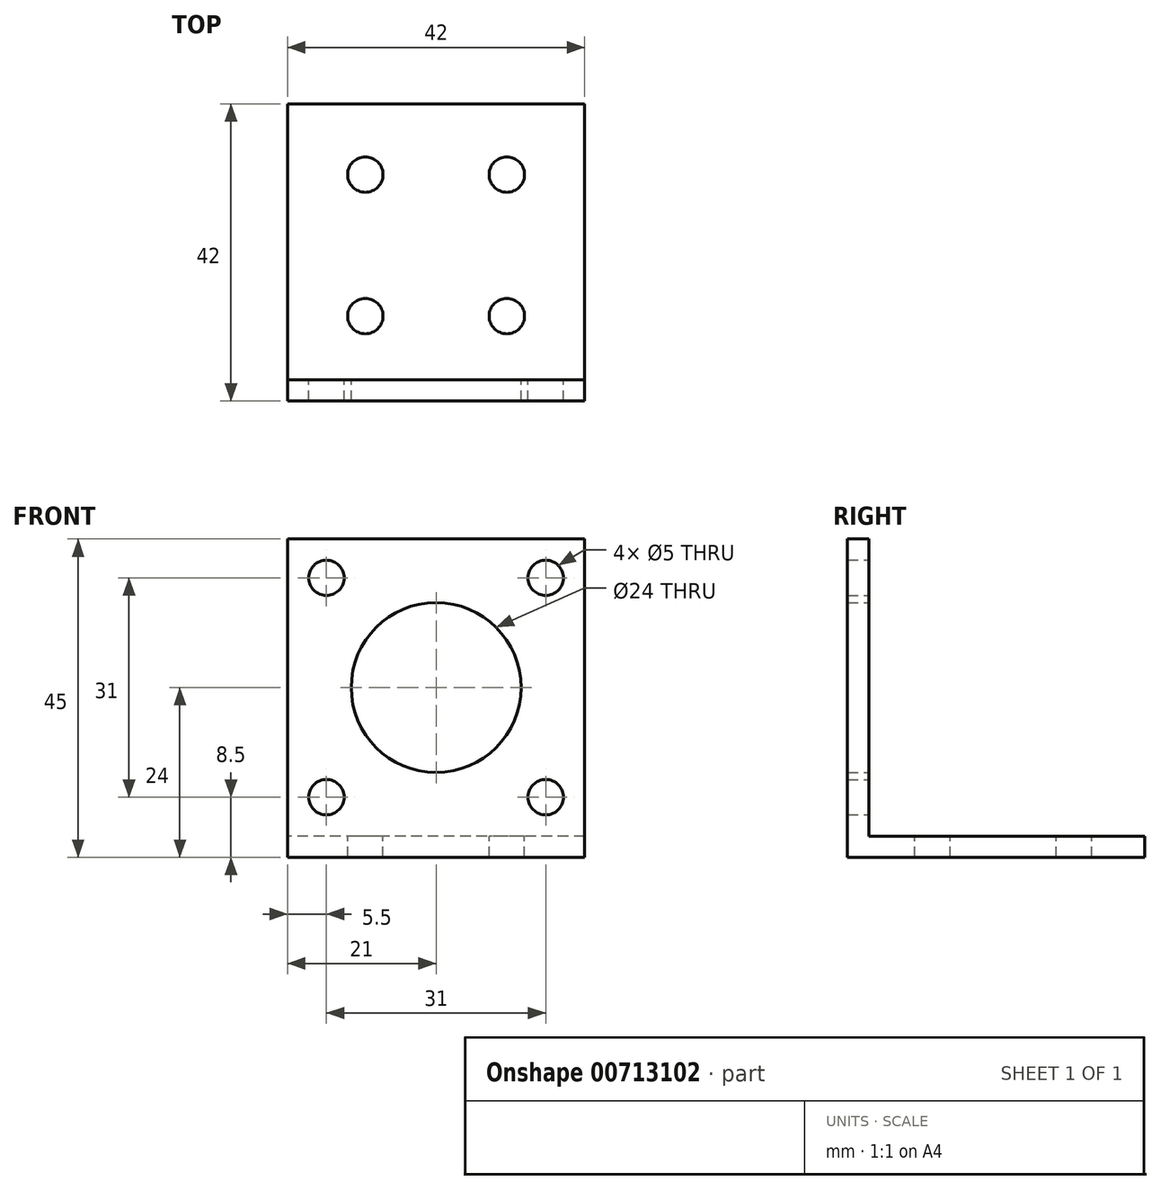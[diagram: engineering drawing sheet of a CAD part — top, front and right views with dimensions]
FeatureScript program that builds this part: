
annotation { "Feature Type Name" : "Feature", "Feature Type Description" : "" }
export const myFeature = defineFeature(function(context is Context, id is Id, definition is map)
    precondition{}
    {
        {
            var Q0;
            Q0=qCreatedBy(makeId("Top.planeOp"),FACE);
            var sketch = newSketch(context, id + "F0", { "sketchPlane" : qUnion([Q0])});
            skLineSegment(sketch, "E0.bottom", {"start": v(21, -21) * mm, "end": v(-21, -21) * mm});
            skLineSegment(sketch, "E0.top", {"start": v(21, 21) * mm, "end": v(-21, 21) * mm});
            skLineSegment(sketch, "E0.left", {"start": v(21, -21) * mm, "end": v(21, 21) * mm});
            skLineSegment(sketch, "E0.right", {"start": v(-21, -21) * mm, "end": v(-21, 21) * mm});
            skPoint(sketch, "E0.middle", {"position": v(0, 0) * mm});
            skLineSegment(sketch, "E1", {"start": v(21, -18) * mm, "end": v(-21, -18) * mm});
            skSolve(sketch);
        }
        {
            var Q0;
            {var subQ0=sQuery(id+"F0.wireOp",EDGE,"E0.top");Q0=makeQuery(id+"F0.imprint","IMPRINT",FACE,{"disambiguationData":[TD([[makeQuery(id+"F0.imprint","IMPRINT",EDGE,{"derivedFrom":subQ0}),1.0]])]});}
            extrude(context, id + "F1", {"entities" : qUnion([Q0]), "depth" : 3 * mm, "offsetDistance" : 25 * mm});
        }
        {
            var Q0;
            {var subQ0=sQuery(id+"F0.wireOp",EDGE,"E0.bottom");Q0=makeQuery(id+"F0.imprint","IMPRINT",FACE,{"disambiguationData":[TD([[makeQuery(id+"F0.imprint","IMPRINT",EDGE,{"derivedFrom":subQ0}),-1.0]])]});}
            extrude(context, id + "F2", {"entities" : qUnion([Q0]), "operationType" : NewBodyOperationType.ADD, "depth" : 45 * mm, "offsetDistance" : 25 * mm});
        }
        {
            var Q0;
            Q0=makeQuery(id+"F1.opExtrude","CAP_FACE",FACE,{"disambiguationData":[OSD([sQuery(id+"F0.wireOp",EDGE,"E0.top"),sQuery(id+"F0.wireOp",EDGE,"E0.left"),sQuery(id+"F0.wireOp",EDGE,"E0.right"),sQuery(id+"F0.wireOp",EDGE,"E1")])],"isStart":false});
            var sketch = newSketch(context, id + "F3", { "sketchPlane" : qUnion([Q0])});
            skLineSegment(sketch, "E2.bottom", {"start": v(10, -9) * mm, "end": v(-10, -9) * mm});
            skLineSegment(sketch, "E2.top", {"start": v(10, 11) * mm, "end": v(-10, 11) * mm});
            skLineSegment(sketch, "E2.left", {"start": v(10, -9) * mm, "end": v(10, 11) * mm});
            skLineSegment(sketch, "E2.right", {"start": v(-10, -9) * mm, "end": v(-10, 11) * mm});
            skSolve(sketch);
        }
        {
            var Q0;
            Q0=sQuery(id+"F3.wireOp",VERTEX,"E2.bottom.start");
            var Q1;
            Q1=sQuery(id+"F3.wireOp",VERTEX,"E2.left.end");
            var Q2;
            Q2=sQuery(id+"F3.wireOp",VERTEX,"E2.top.end");
            var Q3;
            Q3=sQuery(id+"F3.wireOp",VERTEX,"E2.right.start");
            var Q4;
            Q4=makeQuery(id+"F1.opExtrude","SWEPT_BODY",BODY,{"disambiguationData":[OSD([sQuery(id+"F0.wireOp",EDGE,"E0.top"),sQuery(id+"F0.wireOp",EDGE,"E0.left"),sQuery(id+"F0.wireOp",EDGE,"E0.right"),sQuery(id+"F0.wireOp",EDGE,"E1")])]});
            hole(context, id + "F4", {"style" : HoleStyle.SIMPLE, "endStyle" : HoleEndStyle.THROUGH, "holeDiameter" : 5 * mm, "majorDiameter" : 5 * mm, "isTappedThrough" : true, "tappedDepth" : 12 * mm, "tapClearance" : 3, "locations" : qUnion([Q0, Q1, Q2, Q3]), "scope" : qUnion([Q4])});
        }
        {
            var Q0;
            Q0=makeQuery(id+"F2.opExtrude","SWEPT_FACE",FACE,{"disambiguationData":[OSD([sQuery(id+"F0.wireOp",EDGE,"E1")])]});
            var sketch = newSketch(context, id + "F5", { "sketchPlane" : qUnion([Q0])});
            skLineSegment(sketch, "E3.bottom", {"start": v(15.5, 8.5) * mm, "end": v(-15.5, 8.5) * mm});
            skLineSegment(sketch, "E3.top", {"start": v(15.5, 39.5) * mm, "end": v(-15.5, 39.5) * mm});
            skLineSegment(sketch, "E3.left", {"start": v(15.5, 8.5) * mm, "end": v(15.5, 39.5) * mm});
            skLineSegment(sketch, "E3.right", {"start": v(-15.5, 8.5) * mm, "end": v(-15.5, 39.5) * mm});
            skPoint(sketch, "E3.middle", {"position": v(0, 24) * mm});
            skPoint(sketch, "E3.middle.positionSnap0", {"position": v(-21, 24) * mm});
            skPoint(sketch, "E3.centerSnap0", {"position": v(-21, 24) * mm});
            skSolve(sketch);
        }
        {
            var Q0;
            Q0=sQuery(id+"F5.wireOp",VERTEX,"E3.top.end");
            var Q1;
            Q1=sQuery(id+"F5.wireOp",VERTEX,"E3.bottom.end");
            var Q2;
            Q2=sQuery(id+"F5.wireOp",VERTEX,"E3.left.start");
            var Q3;
            Q3=sQuery(id+"F5.wireOp",VERTEX,"E3.top.start");
            var Q4;
            Q4=makeQuery(id+"F1.opExtrude","SWEPT_BODY",BODY,{"disambiguationData":[OSD([sQuery(id+"F0.wireOp",EDGE,"E0.top"),sQuery(id+"F0.wireOp",EDGE,"E0.left"),sQuery(id+"F0.wireOp",EDGE,"E0.right"),sQuery(id+"F0.wireOp",EDGE,"E1")])]});
            hole(context, id + "F6", {"style" : HoleStyle.SIMPLE, "endStyle" : HoleEndStyle.THROUGH, "holeDiameter" : 5 * mm, "majorDiameter" : 5 * mm, "isTappedThrough" : true, "tappedDepth" : 12 * mm, "tapClearance" : 3, "locations" : qUnion([Q0, Q1, Q2, Q3]), "scope" : qUnion([Q4])});
        }
        {
            var Q0;
            Q0=makeQuery(id+"F2.opExtrude","SWEPT_FACE",FACE,{"disambiguationData":[OSD([sQuery(id+"F0.wireOp",EDGE,"E1")])]});
            var sketch = newSketch(context, id + "F7", { "sketchPlane" : qUnion([Q0])});
            skCircle(sketch, "E4", {"center": v(0, 24) * mm, "radius": 12 * mm});
            skPoint(sketch, "E4.centerSnap0", {"position": v(0, 45) * mm});
            skPoint(sketch, "E4.centerSnap1", {"position": v(-21, 24) * mm});
            skSolve(sketch);
        }
        {
            var Q0;
            Q0=makeQuery(id+"F7.imprint","IMPRINT",FACE,{"disambiguationData":[TD([[makeQuery(id+"F7.imprint","IMPRINT",EDGE,{"derivedFrom":sQuery(id+"F7.wireOp",EDGE,"E4")}),1.0]])]});
            extrude(context, id + "F8", {"entities" : qUnion([Q0]), "operationType" : NewBodyOperationType.REMOVE, "oppositeDirection" : true, "depth" : 25 * mm, "offsetDistance" : 25 * mm});
        }
    });
